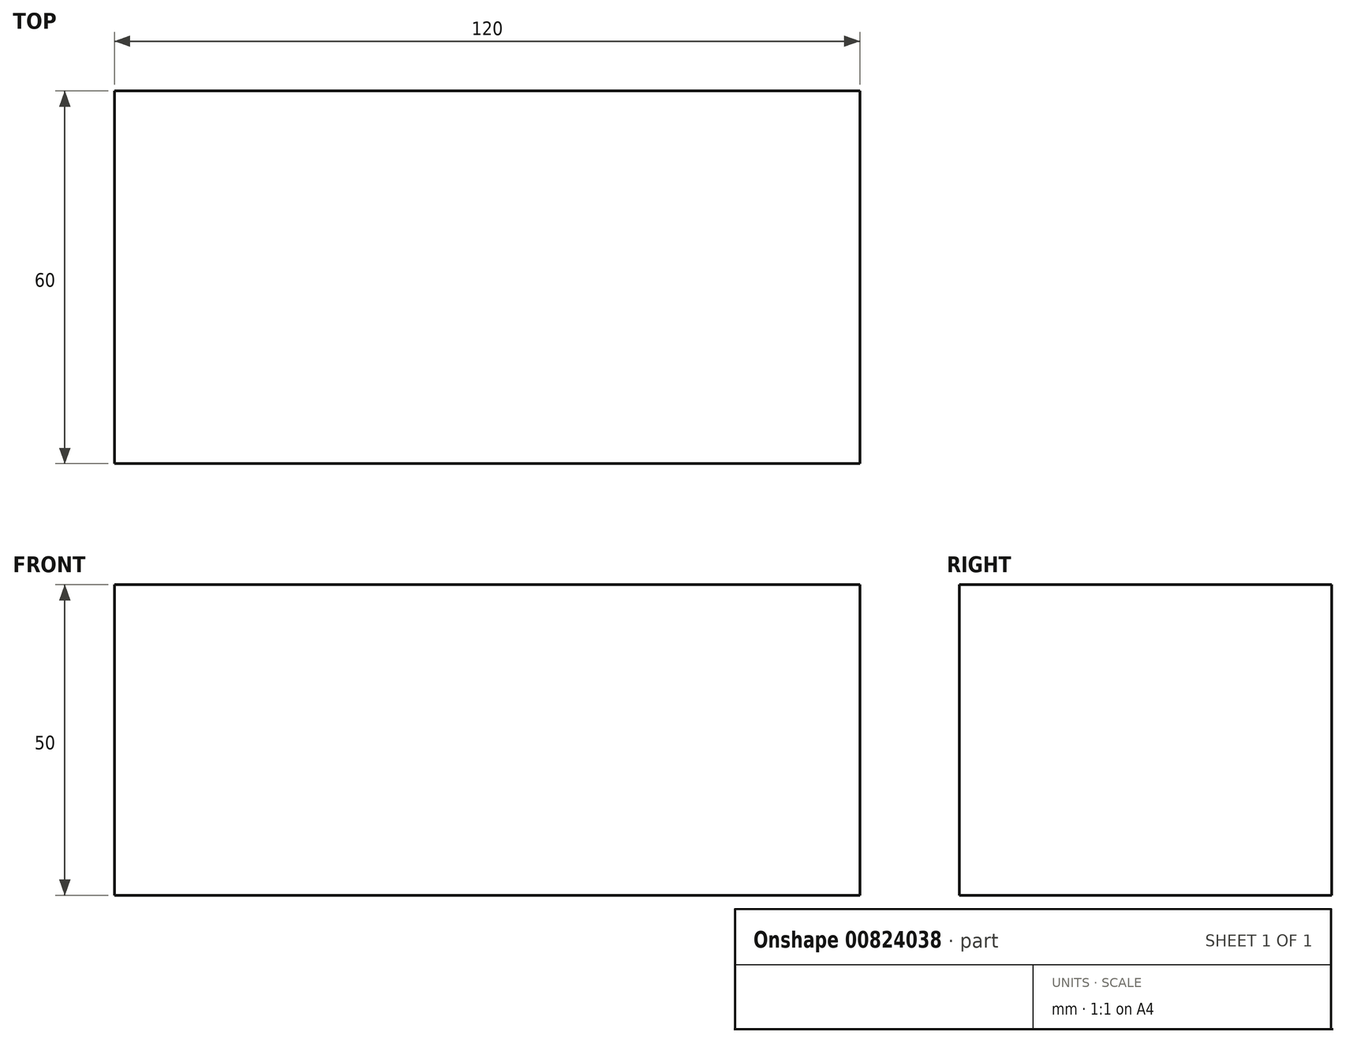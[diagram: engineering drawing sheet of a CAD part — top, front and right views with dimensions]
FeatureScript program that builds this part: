
annotation { "Feature Type Name" : "Feature", "Feature Type Description" : "" }
export const myFeature = defineFeature(function(context is Context, id is Id, definition is map)
    precondition{}
    {
        {
            var Q0;
            Q0=qCreatedBy(makeId("Top.planeOp"),FACE);
            var sketch = newSketch(context, id + "F0", { "sketchPlane" : qUnion([Q0])});
            skLineSegment(sketch, "E0.bottom", {"start": v(60, 30) * mm, "end": v(-60, 30) * mm});
            skLineSegment(sketch, "E0.top", {"start": v(60, -30) * mm, "end": v(-60, -30) * mm});
            skLineSegment(sketch, "E0.left", {"start": v(60, 30) * mm, "end": v(60, -30) * mm});
            skLineSegment(sketch, "E0.right", {"start": v(-60, 30) * mm, "end": v(-60, -30) * mm});
            skPoint(sketch, "E0.middle", {"position": v(0, 0) * mm});
            skSolve(sketch);
        }
        {
            var Q0;
            Q0=makeQuery(id+"F0.imprint","IMPRINT",FACE,{"disambiguationData":[TD([[makeQuery(id+"F0.imprint","IMPRINT",EDGE,{"derivedFrom":sQuery(id+"F0.wireOp",EDGE,"E0.bottom")}),1.0]])]});
            extrude(context, id + "F1", {"entities" : qUnion([Q0]), "depth" : 50 * mm, "offsetDistance" : 25 * mm});
        }
    });
